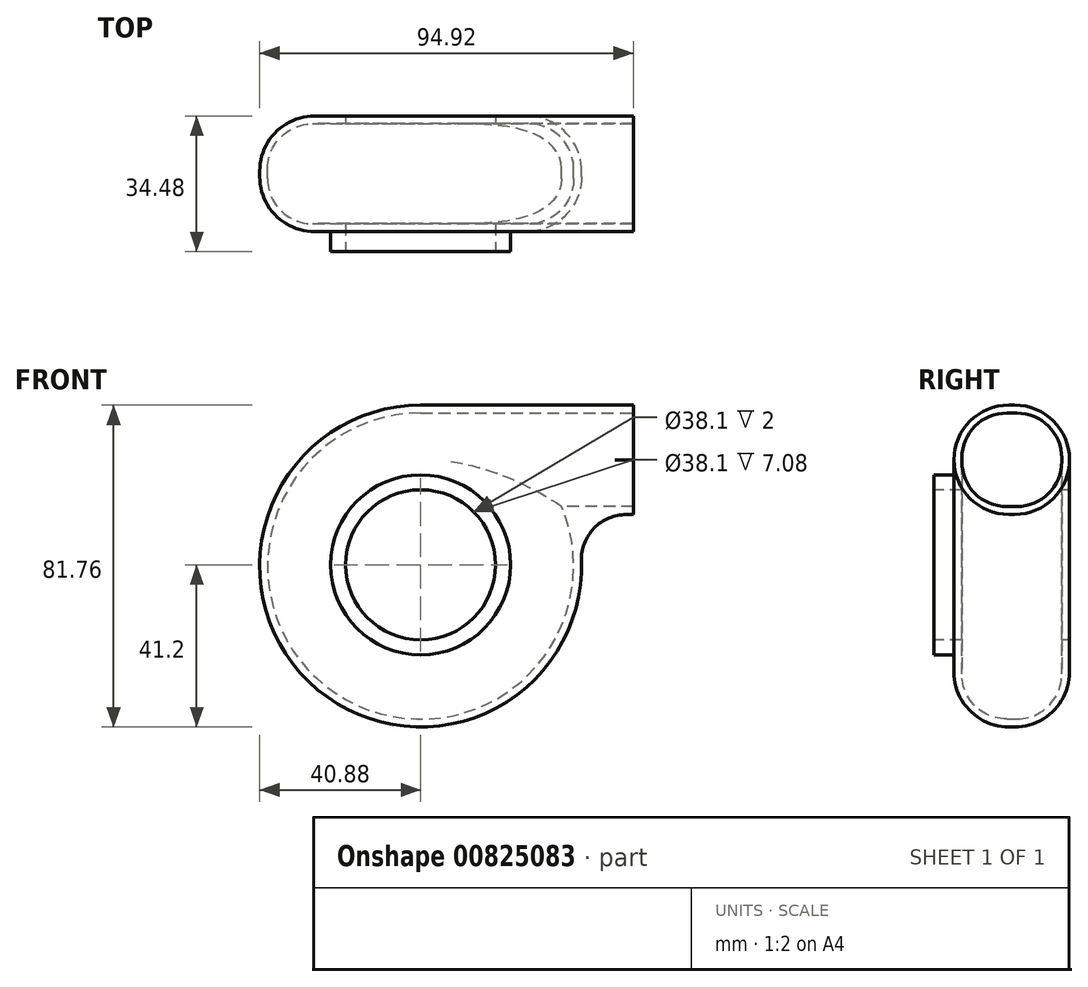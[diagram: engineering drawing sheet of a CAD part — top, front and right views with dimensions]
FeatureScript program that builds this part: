
annotation { "Feature Type Name" : "Feature", "Feature Type Description" : "" }
export const myFeature = defineFeature(function(context is Context, id is Id, definition is map)
    precondition{}
    {
        {
            var Q0;
            Q0=qCreatedBy(makeId("Front.planeOp"),FACE);
            var sketch = newSketch(context, id + "F0", { "sketchPlane" : qUnion([Q0])});
            skCircle(sketch, "E0", {"center": v(0, 0) * mm, "radius": 19.05 * mm});
            skLineSegment(sketch, "E1", {"start": v(0, 35.56) * mm, "end": v(43.42, 35.56) * mm});
            skArc(sketch, "E2", {"start": v(0, 35.56) * mm, "mid": v(-24.74, -26.3) * mm, "end": v(35.83, 1.45) * mm});
            skPoint(sketch, "E2.second.point", {"position": v(-28.5, -22.1) * mm});
            skPoint(sketch, "E2.third.point", {"position": v(-28.5, -22.1) * mm});
            skLineSegment(sketch, "E3", {"start": v(43.42, 35.56) * mm, "end": v(43.42, 17.78) * mm});
            skArc(sketch, "E4.0", {"start": v(0, 38.56) * mm, "mid": v(-21.5, -32.71) * mm, "end": v(35.83, 14.78) * mm});
            skLineSegment(sketch, "E4.1", {"start": v(0, 38.56) * mm, "end": v(46.42, 38.56) * mm});
            skLineSegment(sketch, "E4.2", {"start": v(46.42, 38.56) * mm, "end": v(46.42, 14.78) * mm});
            skLineSegment(sketch, "E4.3", {"start": v(46.42, 14.78) * mm, "end": v(35.83, 14.78) * mm});
            skArc(sketch, "E5", {"start": v(35.88, 0) * mm, "mid": v(33.94, 9.64) * mm, "end": v(28.42, 17.78) * mm});
            skLineSegment(sketch, "E6", {"start": v(28.42, 17.78) * mm, "end": v(43.42, 17.78) * mm});
            skSolve(sketch);
        }
        {
            var Q0;
            Q0=makeQuery(id+"F0.imprint","IMPRINT",FACE,{"disambiguationData":[TD([[makeQuery(id+"F0.imprint","IMPRINT",EDGE,{"derivedFrom":sQuery(id+"F0.wireOp",EDGE,"E0")}),-1.0]])]});
            var Q1;
            {var subQ1=sQuery(id+"F0.wireOp",EDGE,"E1");Q1=makeQuery(id+"F0.imprint","IMPRINT",FACE,{"disambiguationData":[TD([[makeQuery(id+"F0.imprint","IMPRINT",EDGE,{"derivedFrom":subQ1}),1.0]])]});}
            var Q2;
            Q2=makeQuery(id+"F0.imprint","IMPRINT",FACE,{"disambiguationData":[TD([[makeQuery(id+"F0.imprint","IMPRINT",EDGE,{"derivedFrom":sQuery(id+"F0.wireOp",EDGE,"E0")}),1.0]])]});
            extrude(context, id + "F1", {"entities" : qUnion([Q0, Q1, Q2]), "endBound" : BoundingType.SYMMETRIC, "depth" : 25.4 * mm, "offsetDistance" : 25.4 * mm});
        }
        {
            var Q0;
            Q0=makeQuery(id+"F1.opExtrude","SWEPT_FACE",FACE,{"disambiguationData":[OSD([sQuery(id+"F0.wireOp",EDGE,"E4.2")])]});
            shell(context, id + "F2", {"entities" : qUnion([Q0]), "thickness" : 2 * mm, "oppositeDirection" : true});
        }
        {
            var Q0;
            {var subQ0=sQuery(id+"F0.wireOp",EDGE,"E5");var subQ1=sQuery(id+"F0.wireOp",EDGE,"E4.3");var subQ2=sQuery(id+"F0.wireOp",EDGE,"E4.2");var subQ3=sQuery(id+"F0.wireOp",EDGE,"E4.1");var subQ4=sQuery(id+"F0.wireOp",EDGE,"E4.0");var subQ5=sQuery(id+"F0.wireOp",EDGE,"E2");var subQ6=sQuery(id+"F0.wireOp",EDGE,"E0");Q0=makeQuery(id+"F2.opShell","OFFSET_FACE",FACE,{"disambiguationData":[OSD([subQ6,subQ5,subQ4,subQ3,subQ2,subQ1,subQ0]),TDD([makeQuery(id+"F1.opExtrude","CAP_FACE",FACE,{"disambiguationData":[OSD([subQ6,subQ5,subQ4,subQ3,subQ2,subQ1,subQ0])],"isStart":true})])]});}
            var sketch = newSketch(context, id + "F3", { "sketchPlane" : qUnion([Q0])});
            skLineSegment(sketch, "E7.bottom", {"start": v(31.57, 5.3) * mm, "end": v(37.83, 5.3) * mm});
            skLineSegment(sketch, "E7.top", {"start": v(31.57, -3.64) * mm, "end": v(37.83, -3.64) * mm});
            skLineSegment(sketch, "E7.left", {"start": v(31.57, 5.3) * mm, "end": v(31.57, -3.64) * mm});
            skLineSegment(sketch, "E7.right", {"start": v(37.83, 5.3) * mm, "end": v(37.83, -3.64) * mm});
            skSolve(sketch);
        }
        {
            var Q0;
            Q0 = qSketchRegion(id + "F3", true);
            var Q1;
            {var subQ0=sQuery(id+"F0.wireOp",EDGE,"E5");var subQ1=sQuery(id+"F0.wireOp",EDGE,"E4.3");var subQ2=sQuery(id+"F0.wireOp",EDGE,"E4.2");var subQ3=sQuery(id+"F0.wireOp",EDGE,"E4.1");var subQ4=sQuery(id+"F0.wireOp",EDGE,"E4.0");var subQ5=sQuery(id+"F0.wireOp",EDGE,"E2");var subQ6=sQuery(id+"F0.wireOp",EDGE,"E0");Q1=makeQuery(id+"F2.opShell","OFFSET_FACE",FACE,{"disambiguationData":[OSD([subQ6,subQ5,subQ4,subQ3,subQ2,subQ1,subQ0]),TDD([makeQuery(id+"F1.opExtrude","CAP_FACE",FACE,{"disambiguationData":[OSD([subQ6,subQ5,subQ4,subQ3,subQ2,subQ1,subQ0])],"isStart":false})])]});}
            extrude(context, id + "F4", {"entities" : qUnion([Q0]), "operationType" : NewBodyOperationType.REMOVE, "endBound" : BoundingType.UP_TO_SURFACE, "depth" : 36.9 * mm, "endBoundEntityFace" : qUnion([Q1]), "offsetDistance" : 25.4 * mm});
        }
        {
            var Q0;
            Q0=makeQuery(id+"F1.opExtrude","SWEPT_FACE",FACE,{"disambiguationData":[OSD([sQuery(id+"F0.wireOp",EDGE,"E4.2")])]});
            extrude(context, id + "F5", {"entities" : qUnion([Q0]), "operationType" : NewBodyOperationType.ADD, "depth" : 7.62 * mm, "offsetDistance" : 25.4 * mm});
        }
        {
            var Q0;
            {var subQ0=sQuery(id+"F0.wireOp",EDGE,"E4.0");Q0=makeQuery(id+"F2.opShell","OFFSET_EDGE",EDGE,{"disambiguationData":[OSD([subQ0]),TDD([makeQuery(id+"F1.opExtrude","CAP_EDGE",EDGE,{"disambiguationData":[OSD([subQ0])],"isStart":true})])]});}
            var Q1;
            {var subQ0=sQuery(id+"F0.wireOp",EDGE,"E4.3");Q1=makeQuery(id+"F2.opShell","OFFSET_EDGE",EDGE,{"disambiguationData":[OSD([subQ0]),TDD([makeQuery(id+"F1.opExtrude","CAP_EDGE",EDGE,{"disambiguationData":[OSD([subQ0])],"isStart":true})])]});}
            var Q2;
            {var subQ0=sQuery(id+"F0.wireOp",EDGE,"E4.0");Q2=makeQuery(id+"F2.opShell","OFFSET_EDGE",EDGE,{"disambiguationData":[OSD([subQ0]),TDD([makeQuery(id+"F1.opExtrude","CAP_EDGE",EDGE,{"disambiguationData":[OSD([subQ0])],"isStart":false})])]});}
            var Q3;
            Q3=makeQuery(id+"F1.opExtrude","SWEPT_EDGE",EDGE,{"disambiguationData":[OSD([sQuery(id+"F0.wireOp",EDGE,"E4.0"),sQuery(id+"F0.wireOp",EDGE,"E4.3")])]});
            var Q4;
            {var subQ0=sQuery(id+"F0.wireOp",EDGE,"E4.3");var subQ1=sQuery(id+"F0.wireOp",EDGE,"E4.2");Q4=makeQuery(id+"F5.boolean.opBoolean","MERGE",EDGE,{"derivedFrom":[makeQuery(id+"F2.opShell","OFFSET_EDGE",EDGE,{"disambiguationData":[OSD([subQ0]),TDD([makeQuery(id+"F1.opExtrude","CAP_EDGE",EDGE,{"disambiguationData":[OSD([subQ0])],"isStart":false})])]}),makeQuery(id+"F5.opExtrude","SWEPT_EDGE",EDGE,{"disambiguationData":[OSD([subQ1,subQ0]),TDD([makeQuery(id+"F2.opShell","OFFSET_VERTEX",VERTEX,{"disambiguationData":[OSD([subQ1,subQ0]),TDD([makeQuery(id+"F1.opExtrude","CAP_VERTEX",VERTEX,{"disambiguationData":[OSD([subQ1,subQ0])],"isStart":false})])]})])]})]});}
            fillet(context, id + "F6", {"entities" : qUnion([Q0, Q1, Q2, Q3, Q4]), "radius" : 11.43 * mm, "tangentPropagation" : true, "allowEdgeOverflow" : false});
        }
        {
            var Q0;
            Q0=makeQuery(id+"F1.opExtrude","CAP_EDGE",EDGE,{"disambiguationData":[OSD([sQuery(id+"F0.wireOp",EDGE,"E4.1")])],"isStart":true});
            var Q1;
            {var subQ0=sQuery(id+"F0.wireOp",EDGE,"E4.2");var subQ1=sQuery(id+"F0.wireOp",EDGE,"E4.1");Q1=makeQuery(id+"F5.boolean.opBoolean","MERGE",EDGE,{"derivedFrom":[makeQuery(id+"F1.opExtrude","CAP_EDGE",EDGE,{"disambiguationData":[OSD([subQ1])],"isStart":false}),makeQuery(id+"F5.opExtrude","SWEPT_EDGE",EDGE,{"disambiguationData":[OSD([subQ1,subQ0]),TDD([makeQuery(id+"F1.opExtrude","CAP_VERTEX",VERTEX,{"disambiguationData":[OSD([subQ1,subQ0])],"isStart":false})])]})]});}
            fillet(context, id + "F7", {"entities" : qUnion([Q0, Q1]), "radius" : 13.97 * mm, "tangentPropagation" : true, "allowEdgeOverflow" : false});
        }
        {
            var Q0;
            {var subQ0=sQuery(id+"F0.wireOp",EDGE,"E4.2");Q0=makeQuery(id+"F5.boolean.opBoolean","MERGE",FACE,{"derivedFrom":[makeQuery(id+"F1.opExtrude","CAP_FACE",FACE,{"disambiguationData":[OSD([sQuery(id+"F0.wireOp",EDGE,"E2"),sQuery(id+"F0.wireOp",EDGE,"E4.0"),sQuery(id+"F0.wireOp",EDGE,"E4.1"),subQ0,sQuery(id+"F0.wireOp",EDGE,"E4.3"),sQuery(id+"F0.wireOp",EDGE,"E5")])],"isStart":false}),makeQuery(id+"F5.opExtrude","SWEPT_FACE",FACE,{"disambiguationData":[OSD([subQ0]),TDD([makeQuery(id+"F1.opExtrude","CAP_EDGE",EDGE,{"disambiguationData":[OSD([subQ0])],"isStart":false})])]})]});}
            var sketch = newSketch(context, id + "F8", { "sketchPlane" : qUnion([Q0])});
            skCircle(sketch, "E8", {"center": v(0, 0) * mm, "radius": 19.05 * mm});
            skSolve(sketch);
        }
        {
            var Q0;
            Q0=makeQuery(id+"F8.imprint","IMPRINT",FACE,{"disambiguationData":[TD([[makeQuery(id+"F8.imprint","IMPRINT",EDGE,{"derivedFrom":sQuery(id+"F8.wireOp",EDGE,"E8")}),1.0]])]});
            extrude(context, id + "F9", {"entities" : qUnion([Q0]), "operationType" : NewBodyOperationType.REMOVE, "endBound" : BoundingType.THROUGH_ALL, "oppositeDirection" : true, "depth" : 25.4 * mm, "offsetDistance" : 25.4 * mm});
        }
        {
            var Q0;
            {var subQ0=sQuery(id+"F0.wireOp",EDGE,"E4.2");Q0=makeQuery(id+"F5.boolean.opBoolean","MERGE",FACE,{"derivedFrom":[makeQuery(id+"F1.opExtrude","CAP_FACE",FACE,{"disambiguationData":[OSD([sQuery(id+"F0.wireOp",EDGE,"E2"),sQuery(id+"F0.wireOp",EDGE,"E4.0"),sQuery(id+"F0.wireOp",EDGE,"E4.1"),subQ0,sQuery(id+"F0.wireOp",EDGE,"E4.3"),sQuery(id+"F0.wireOp",EDGE,"E5")])],"isStart":false}),makeQuery(id+"F5.opExtrude","SWEPT_FACE",FACE,{"disambiguationData":[OSD([subQ0]),TDD([makeQuery(id+"F1.opExtrude","CAP_EDGE",EDGE,{"disambiguationData":[OSD([subQ0])],"isStart":false})])]})]});}
            var sketch = newSketch(context, id + "F10", { "sketchPlane" : qUnion([Q0])});
            skCircle(sketch, "E9", {"center": v(0, 0) * mm, "radius": 22.86 * mm});
            skSolve(sketch);
        }
        {
            var Q0;
            Q0=makeQuery(id+"F10.imprint","IMPRINT",FACE,{"disambiguationData":[TD([[makeQuery(id+"F10.imprint","IMPRINT",EDGE,{"derivedFrom":sQuery(id+"F10.wireOp",EDGE,"E9")}),1.0]])]});
            extrude(context, id + "F11", {"entities" : qUnion([Q0]), "operationType" : NewBodyOperationType.ADD, "depth" : 5.08 * mm, "offsetDistance" : 25.4 * mm});
        }
    });
